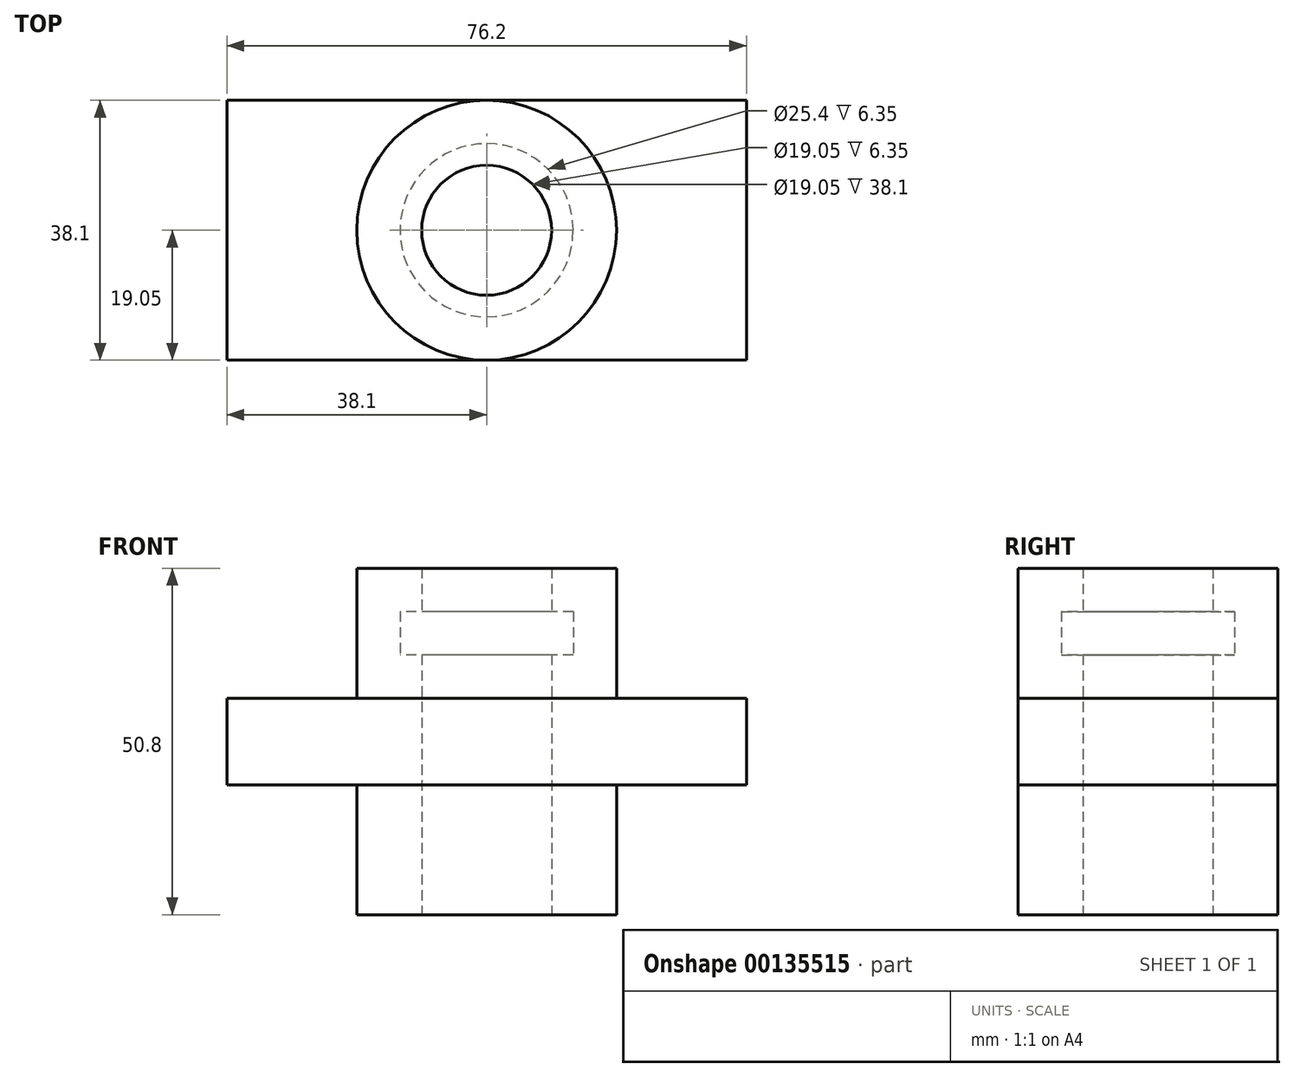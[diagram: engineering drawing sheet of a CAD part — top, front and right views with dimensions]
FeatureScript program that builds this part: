
annotation { "Feature Type Name" : "Feature", "Feature Type Description" : "" }
export const myFeature = defineFeature(function(context is Context, id is Id, definition is map)
    precondition{}
    {
        {
            var Q0;
            Q0=qCreatedBy(makeId("Top.planeOp"),FACE);
            var sketch = newSketch(context, id + "F0", { "sketchPlane" : qUnion([Q0])});
            skCircle(sketch, "E0", {"center": v(0, 0) * mm, "radius": 19.05 * mm});
            skCircle(sketch, "E1", {"center": v(0, 0) * mm, "radius": 9.53 * mm});
            skSolve(sketch);
        }
        {
            var Q0;
            Q0 = qSketchRegion(id + "F0", true);
            extrude(context, id + "F1", {"entities" : qUnion([Q0]), "depth" : 38.1 * mm});
        }
        {
            var Q0;
            Q0=makeQuery(id+"F1.opExtrude","CAP_FACE",FACE,{"disambiguationData":[OSD([sQuery(id+"F0.wireOp",EDGE,"E0"),sQuery(id+"F0.wireOp",EDGE,"E1")])],"isStart":false});
            var sketch = newSketch(context, id + "F2", { "sketchPlane" : qUnion([Q0])});
            skCircle(sketch, "E2.0", {"center": v(0, 0) * mm, "radius": 19.05 * mm});
            skCircle(sketch, "E3", {"center": v(0, 0) * mm, "radius": 12.7 * mm});
            skSolve(sketch);
        }
        {
            var Q0;
            Q0 = qSketchRegion(id + "F2", true);
            extrude(context, id + "F3", {"entities" : qUnion([Q0]), "operationType" : NewBodyOperationType.ADD, "depth" : 6.35 * mm});
        }
        {
            var Q0;
            Q0=makeQuery(id+"F3.opExtrude","CAP_FACE",FACE,{"disambiguationData":[OSD([sQuery(id+"F2.wireOp",EDGE,"E2.0"),sQuery(id+"F2.wireOp",EDGE,"E3")])],"isStart":false});
            var sketch = newSketch(context, id + "F4", { "sketchPlane" : qUnion([Q0])});
            skCircle(sketch, "E4.0", {"center": v(0, 0) * mm, "radius": 19.05 * mm});
            skCircle(sketch, "E5.0", {"center": v(0, 0) * mm, "radius": 9.53 * mm});
            skSolve(sketch);
        }
        {
            var Q0;
            Q0 = qSketchRegion(id + "F4", true);
            extrude(context, id + "F5", {"entities" : qUnion([Q0]), "operationType" : NewBodyOperationType.ADD, "depth" : 6.35 * mm});
        }
        {
            var Q0;
            Q0=qCreatedBy(makeId("Right.planeOp"),FACE);
            var sketch = newSketch(context, id + "F6", { "sketchPlane" : qUnion([Q0])});
            skLineSegment(sketch, "E6.bottom", {"start": v(19.05, 31.75) * mm, "end": v(-19.05, 31.75) * mm});
            skLineSegment(sketch, "E6.top", {"start": v(19.05, 19.05) * mm, "end": v(-19.05, 19.05) * mm});
            skLineSegment(sketch, "E6.left", {"start": v(19.05, 31.75) * mm, "end": v(19.05, 19.05) * mm});
            skLineSegment(sketch, "E6.right", {"start": v(-19.05, 31.75) * mm, "end": v(-19.05, 19.05) * mm});
            skPoint(sketch, "E6.middle", {"position": v(0, 25.4) * mm});
            skSolve(sketch);
        }
        {
            var Q0;
            Q0 = qSketchRegion(id + "F6", true);
            extrude(context, id + "F7", {"entities" : qUnion([Q0]), "operationType" : NewBodyOperationType.ADD, "endBound" : BoundingType.SYMMETRIC, "depth" : 76.2 * mm});
        }
        {
            var Q0;
            Q0=makeQuery(id+"F5.opExtrude","CAP_FACE",FACE,{"disambiguationData":[OSD([sQuery(id+"F4.wireOp",EDGE,"E4.0"),sQuery(id+"F4.wireOp",EDGE,"E5.0")])],"isStart":false});
            var sketch = newSketch(context, id + "F8", { "sketchPlane" : qUnion([Q0])});
            skCircle(sketch, "E7.0", {"center": v(0, 0) * mm, "radius": 9.53 * mm});
            skSolve(sketch);
        }
        {
            var Q0;
            Q0 = qSketchRegion(id + "F8", true);
            extrude(context, id + "F9", {"entities" : qUnion([Q0]), "operationType" : NewBodyOperationType.REMOVE, "endBound" : BoundingType.THROUGH_ALL, "oppositeDirection" : true, "depth" : 25.4 * mm});
        }
    });
